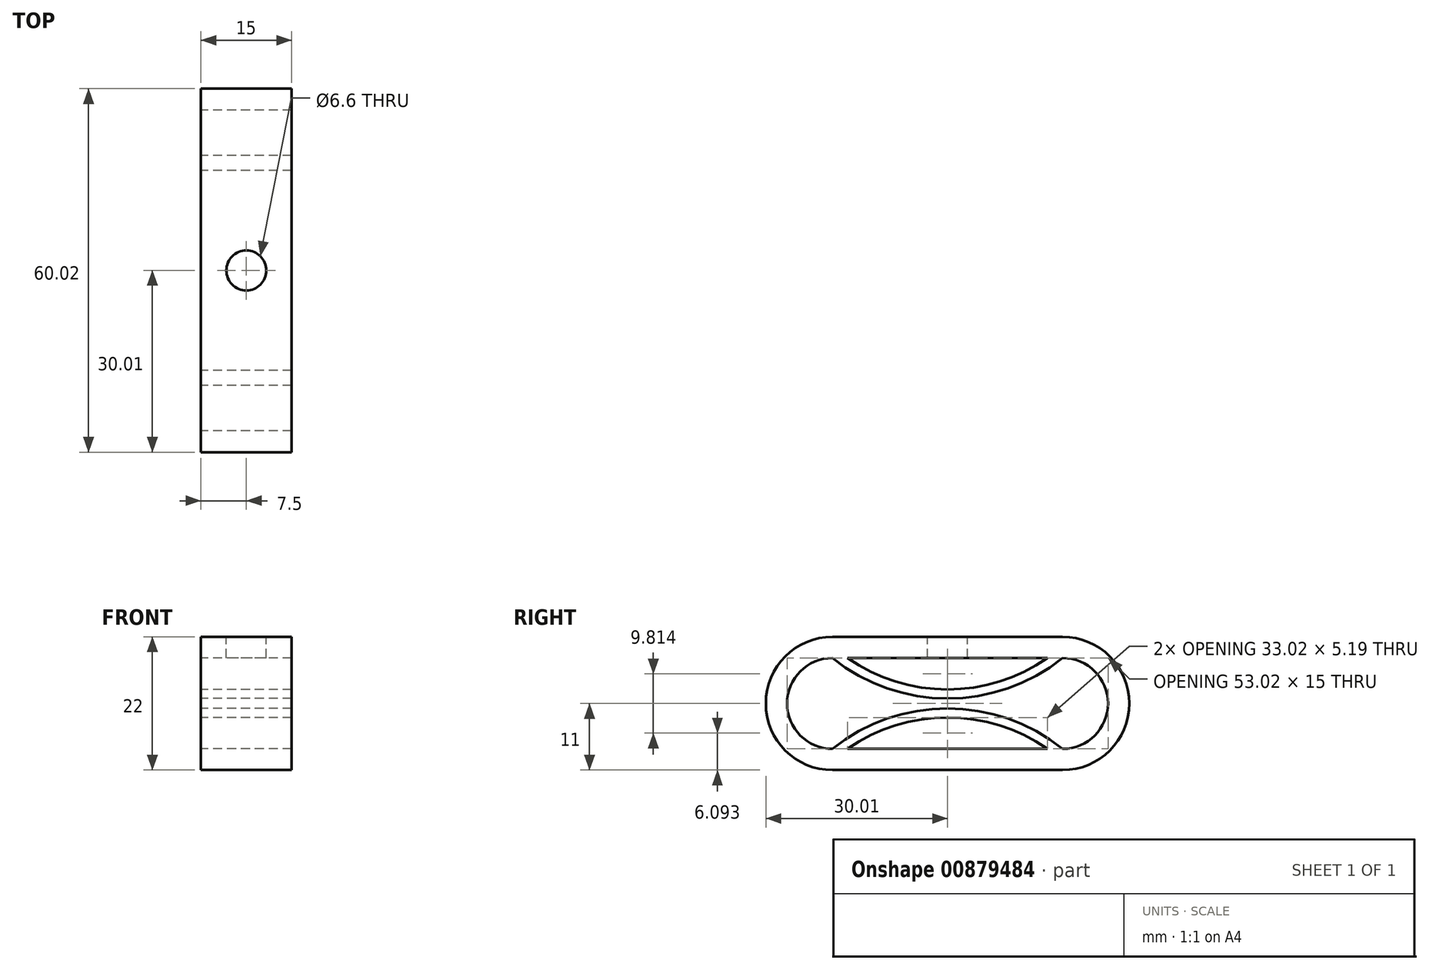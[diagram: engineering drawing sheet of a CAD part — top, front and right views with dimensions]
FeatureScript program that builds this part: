
annotation { "Feature Type Name" : "Feature", "Feature Type Description" : "" }
export const myFeature = defineFeature(function(context is Context, id is Id, definition is map)
    precondition{}
    {
        {
            var Q0;
            Q0=qCreatedBy(makeId("Right.planeOp"),FACE);
            var sketch = newSketch(context, id + "F0", { "sketchPlane" : qUnion([Q0])});
            skArc(sketch, "E0", {"start": v(-19.01, 7.5) * mm, "mid": v(-26.51, 0) * mm, "end": v(-19.01, -7.5) * mm});
            skArc(sketch, "E1.MirrorC", {"start": v(19.01, 7.5) * mm, "mid": v(26.51, 0) * mm, "end": v(19.01, -7.5) * mm});
            skLineSegment(sketch, "E2", {"start": v(-16.5, 7.5) * mm, "end": v(16.5, 7.5) * mm});
            skLineSegment(sketch, "E3.MirrorCS", {"start": v(-16.5, -7.5) * mm, "end": v(16.5, -7.5) * mm});
            skArc(sketch, "E4.0", {"start": v(-19.01, 11) * mm, "mid": v(-30.01, 0) * mm, "end": v(-19.01, -11) * mm});
            skLineSegment(sketch, "E4.1", {"start": v(-19.01, 11) * mm, "end": v(19.01, 11) * mm});
            skArc(sketch, "E4.2", {"start": v(19.01, 11) * mm, "mid": v(30.01, 0) * mm, "end": v(19.01, -11) * mm});
            skLineSegment(sketch, "E4.3", {"start": v(-19.01, -11) * mm, "end": v(19.01, -11) * mm});
            skArc(sketch, "E5", {"start": v(-19.01, 7.5) * mm, "mid": v(0, 0.81) * mm, "end": v(19.01, 7.5) * mm});
            skArc(sketch, "E6.0", {"start": v(-16.5, 7.5) * mm, "mid": v(0, 2.31) * mm, "end": v(16.5, 7.5) * mm});
            skArc(sketch, "E7.MirrorCS", {"start": v(-19.01, -7.5) * mm, "mid": v(0, -0.81) * mm, "end": v(19.01, -7.5) * mm});
            skArc(sketch, "E8.MirrorCS", {"start": v(-16.5, -7.5) * mm, "mid": v(0, -2.31) * mm, "end": v(16.5, -7.5) * mm});
            skSolve(sketch);
        }
        {
            var Q0;
            Q0=makeQuery(id+"F0.imprint","IMPRINT",FACE,{"disambiguationData":[TD([[makeQuery(id+"F0.imprint","IMPRINT",EDGE,{"derivedFrom":sQuery(id+"F0.wireOp",EDGE,"E0")}),-1.0]])]});
            extrude(context, id + "F1", {"entities" : qUnion([Q0]), "endBound" : BoundingType.SYMMETRIC, "depth" : 15 * mm, "offsetDistance" : 25 * mm});
        }
        {
            var Q0;
            Q0=makeQuery(id+"F1.opExtrude","SWEPT_FACE",FACE,{"disambiguationData":[OSD([sQuery(id+"F0.wireOp",EDGE,"E4.1")])]});
            var sketch = newSketch(context, id + "F2", { "sketchPlane" : qUnion([Q0])});
            skPoint(sketch, "E9", {"position": v(0, 0) * mm});
            skSolve(sketch);
        }
        {
            var Q0;
            Q0=sQuery(id+"F2.wireOp",VERTEX,"E9");
            var Q1;
            Q1=makeQuery(id+"F1.opExtrude","SWEPT_BODY",BODY,{"disambiguationData":[OSD([sQuery(id+"F0.wireOp",EDGE,"E0"),sQuery(id+"F0.wireOp",EDGE,"E1.MirrorC"),sQuery(id+"F0.wireOp",EDGE,"E2"),sQuery(id+"F0.wireOp",EDGE,"E3.MirrorCS"),sQuery(id+"F0.wireOp",EDGE,"E4.0"),sQuery(id+"F0.wireOp",EDGE,"E4.1"),sQuery(id+"F0.wireOp",EDGE,"E4.2"),sQuery(id+"F0.wireOp",EDGE,"E4.3"),sQuery(id+"F0.wireOp",EDGE,"E5"),sQuery(id+"F0.wireOp",EDGE,"E6.0"),sQuery(id+"F0.wireOp",EDGE,"E7.MirrorCS"),sQuery(id+"F0.wireOp",EDGE,"E8.MirrorCS")])]});
            hole(context, id + "F3", {"style" : HoleStyle.SIMPLE, "endStyle" : HoleEndStyle.BLIND, "holeDiameter" : 6.6 * mm, "majorDiameter" : 5 * mm, "holeDepth" : 4 * mm, "isTappedThrough" : true, "tappedDepth" : 12 * mm, "tapClearance" : 3, "locations" : qUnion([Q0]), "scope" : qUnion([Q1])});
        }
    });
